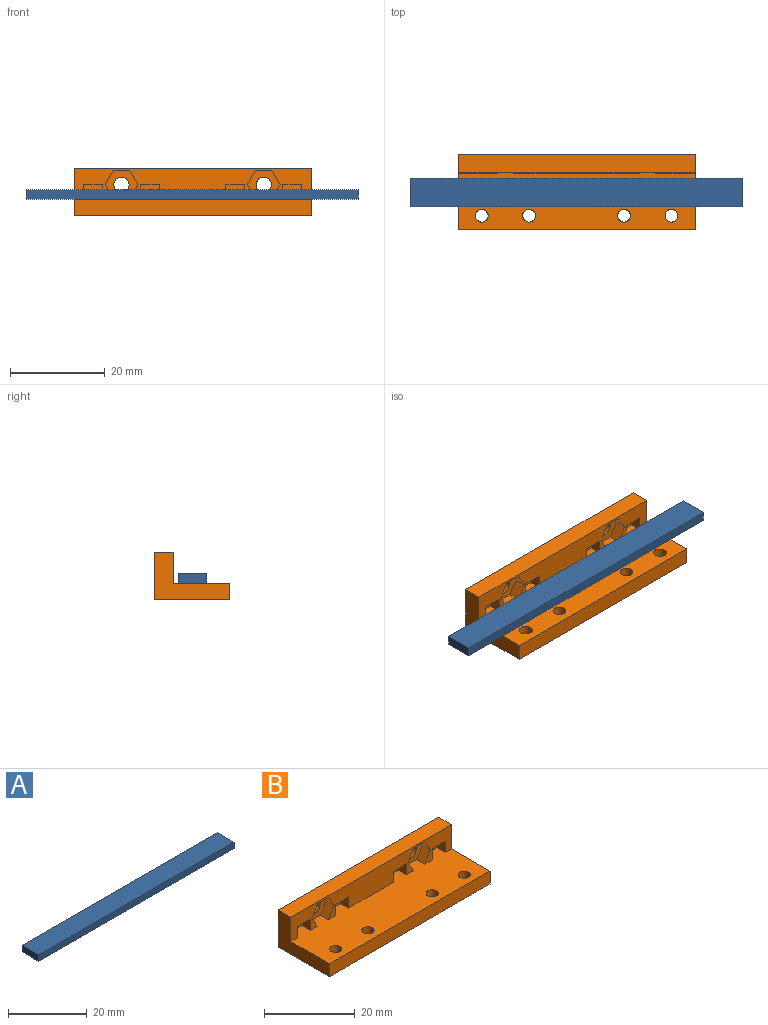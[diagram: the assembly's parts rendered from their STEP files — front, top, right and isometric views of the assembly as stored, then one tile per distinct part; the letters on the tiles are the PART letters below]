
ASSEMBLY  parts=2 mates=1
PART A: 6 faces, bbox 70x6x2 mm
  f0: plane 70x6mm, normal (0,0,1), area 420mm2, adj f1,f3,f4,f5
  f1: plane 70x2mm, normal (0,-1,0), area 140mm2, adj f0,f2,f4,f5
  f2: plane 70x6mm, normal (0,0,-1), area 420mm2, adj f1,f3,f4,f5
  f3: plane 70x2mm, normal (0,1,0), area 140mm2, adj f0,f2,f4,f5
  f4: plane 6x2mm, normal (1,0,0), area 12mm2, adj f0,f1,f2,f3
  f5: plane 6x2mm, normal (-1,0,0), area 12mm2, adj f0,f1,f2,f3
PART B: 42 faces, bbox 50x16x10 mm
  f0: cylinder r=1.6mm len=3.2mm, axis (0,1,0), area 15.1mm2, adj f9,f19
  f1: cylinder r=1.6mm len=3.2mm, axis (0,1,0), area 15.1mm2, adj f9,f37
  f2: plane 50x6.5mm, normal (0,-1,0), area 214.6mm2, adj f4,f6,f7,f8,f14,f15,f16,f17
  f3: plane 50x16mm, normal (0,0,-1), area 777.1mm2, adj f5,f7,f8,f9,f10,f11,f12,f13
  f4: plane 50x14.5mm, normal (0,0,1), area 634.4mm2, adj f2,f5,f7,f8,f10,f11,f12,f13
  f5: plane 50x3.5mm, normal (0,-1,0), area 175mm2, adj f3,f4,f7,f8
  f6: plane 50x4mm, normal (0,0,1), area 200mm2, adj f2,f7,f8,f9
  f7: plane 16x10mm, normal (-1,0,0), area 82mm2, adj f2,f3,f4,f5,f6,f9
  f8: plane 16x10mm, normal (1,0,0), area 82mm2, adj f2,f3,f4,f5,f6,f9
  f9: plane 50x10mm, normal (0,1,0), area 483.9mm2, adj f0,f1,f3,f6,f7,f8
  f10: cylinder r=1.35mm len=3.5mm, axis (0,0,1), area 29.7mm2, adj f3,f4
  f11: cylinder r=1.35mm len=3.5mm, axis (0,0,1), area 29.7mm2, adj f3,f4
  f12: cylinder r=1.35mm len=3.5mm, axis (0,0,1), area 29.7mm2, adj f3,f4
  f13: cylinder r=1.35mm len=3.5mm, axis (0,0,1), area 29.7mm2, adj f3,f4
  f14: plane 3x2.5mm, normal (0.87,0,0.5), area 8.7mm2, adj f2,f4,f18,f19
  f15: plane 3x2.5mm, normal (-0.87,0,0.5), area 8.7mm2, adj f2,f4,f16,f19
  f16: plane 3x2.5mm, normal (-0.87,0,-0.5), area 8.7mm2, adj f2,f15,f17,f19
  f17: plane 3.46x2.5mm, normal (0,0,-1), area 8.7mm2, adj f2,f16,f18,f19
  f18: plane 3x2.5mm, normal (0.87,0,-0.5), area 8.7mm2, adj f2,f14,f17,f19
  f19: plane 6.93x6mm, normal (0,-1,0), area 23.1mm2, adj f0,f4,f14,f15,f16,f17,f18
  f20: plane 3x2.5mm, normal (1,0,0), area 7.5mm2, adj f2,f4,f22,f23
  f21: plane 3x2.5mm, normal (-1,0,0), area 7.5mm2, adj f2,f4,f22,f23
  f22: plane 4x2.5mm, normal (0,0,-1), area 10mm2, adj f2,f20,f21,f23
  f23: plane 4x3mm, normal (0,-1,0), area 12mm2, adj f4,f20,f21,f22
  f24: plane 3x2.5mm, normal (-1,0,0), area 7.5mm2, adj f2,f4,f25,f27
  f25: plane 4x2.5mm, normal (0,0,-1), area 10mm2, adj f2,f24,f26,f27
  f26: plane 3x2.5mm, normal (1,0,0), area 7.5mm2, adj f2,f4,f25,f27
  f27: plane 4x3mm, normal (0,-1,0), area 12mm2, adj f4,f24,f25,f26
  f28: plane 3x2.5mm, normal (1,0,0), area 7.5mm2, adj f2,f4,f30,f31
  f29: plane 3x2.5mm, normal (-1,0,0), area 7.5mm2, adj f2,f4,f30,f31
  f30: plane 4x2.5mm, normal (0,0,-1), area 10mm2, adj f2,f28,f29,f31
  f31: plane 4x3mm, normal (0,-1,0), area 12mm2, adj f4,f28,f29,f30
  f32: plane 3x2.5mm, normal (0.87,0,-0.5), area 8.7mm2, adj f2,f33,f36,f37
  f33: plane 3x2.5mm, normal (0.87,0,0.5), area 8.7mm2, adj f2,f4,f32,f37
  f34: plane 3x2.5mm, normal (-0.87,0,0.5), area 8.7mm2, adj f2,f4,f35,f37
  f35: plane 3x2.5mm, normal (-0.87,0,-0.5), area 8.7mm2, adj f2,f34,f36,f37
  f36: plane 3.46x2.5mm, normal (0,0,-1), area 8.7mm2, adj f2,f32,f35,f37
  f37: plane 6.93x6mm, normal (0,-1,0), area 23.1mm2, adj f1,f4,f32,f33,f34,f35,f36
  f38: plane 3x2.5mm, normal (1,0,0), area 7.5mm2, adj f2,f4,f40,f41
  f39: plane 3x2.5mm, normal (-1,0,0), area 7.5mm2, adj f2,f4,f40,f41
  f40: plane 4x2.5mm, normal (0,0,-1), area 10mm2, adj f2,f38,f39,f41
  f41: plane 4x3mm, normal (0,-1,0), area 12mm2, adj f4,f38,f39,f40
PLACE A t=(8.88,2.02,3.61)mm
PLACE B t=(9,13.09,-1.89)mm
MATE planar B.f4 <-> A.f2  axis (0,0,1) through (9,3.86,1.61)mm
